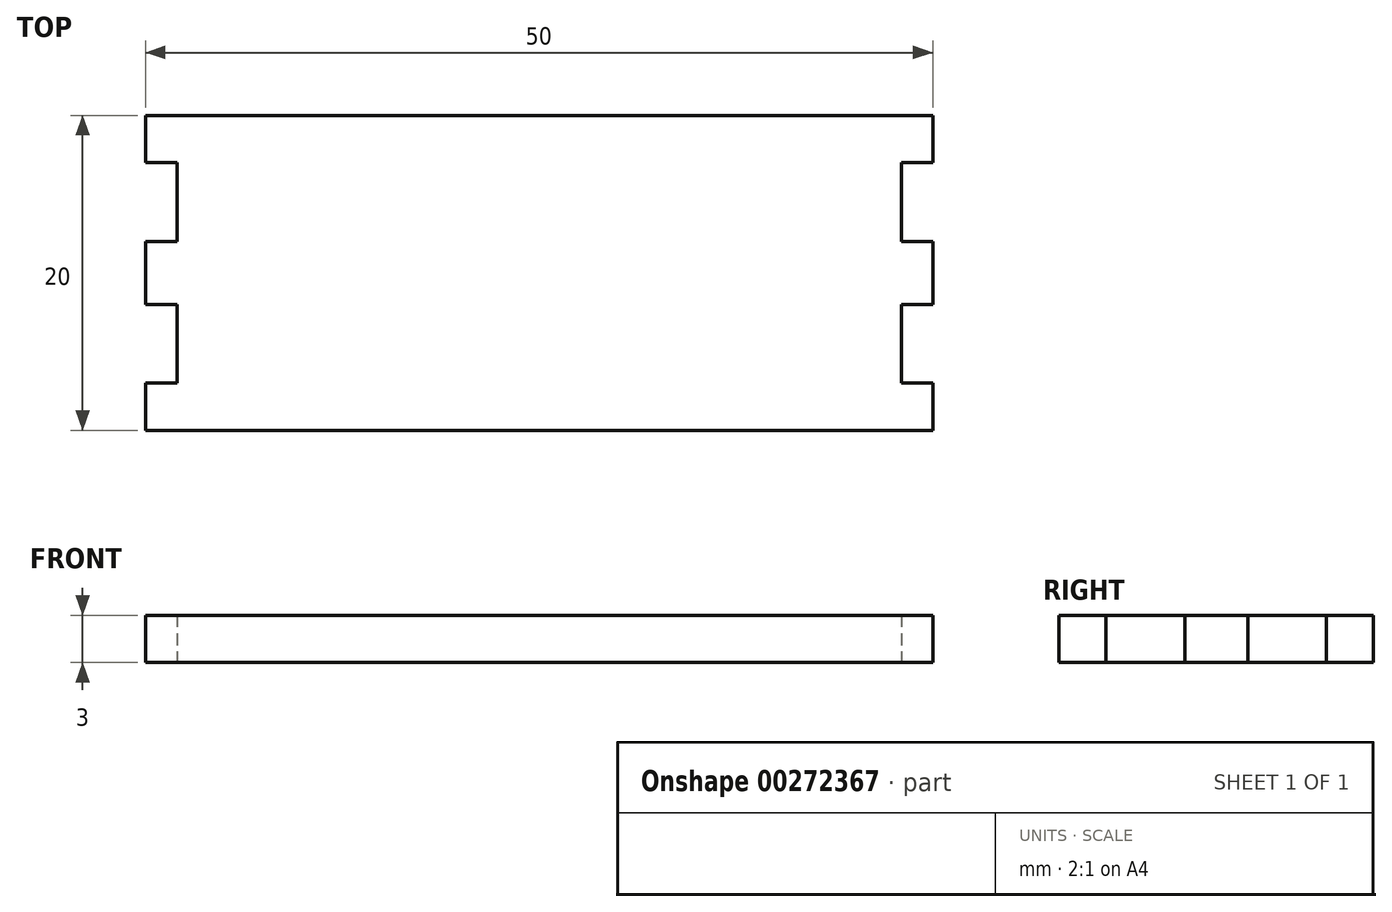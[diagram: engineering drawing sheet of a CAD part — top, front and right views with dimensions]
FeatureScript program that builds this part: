
annotation { "Feature Type Name" : "Feature", "Feature Type Description" : "" }
export const myFeature = defineFeature(function(context is Context, id is Id, definition is map)
    precondition{}
    {
        {
            var Q0;
            Q0=qCreatedBy(makeId("Top.planeOp"),FACE);
            var sketch = newSketch(context, id + "F0", { "sketchPlane" : qUnion([Q0])});
            skLineSegment(sketch, "E0.bottom", {"start": v(-25, 10) * mm, "end": v(25, 10) * mm});
            skLineSegment(sketch, "E0.top", {"start": v(-25, -10) * mm, "end": v(25, -10) * mm});
            skPoint(sketch, "E0.middle", {"position": v(0, 0) * mm});
            skLineSegment(sketch, "E1", {"start": v(0, 10) * mm, "end": v(0, -10) * mm, "construction": true});
            skLineSegment(sketch, "E2", {"start": v(-25, 0) * mm, "end": v(25, 0) * mm, "construction": true});
            skLineSegment(sketch, "E3", {"start": v(-25, 10) * mm, "end": v(-25, 7) * mm});
            skLineSegment(sketch, "E4", {"start": v(-25, 7) * mm, "end": v(-23, 7) * mm});
            skLineSegment(sketch, "E5", {"start": v(-23, 7) * mm, "end": v(-23, 2) * mm});
            skLineSegment(sketch, "E6", {"start": v(-23, 2) * mm, "end": v(-25, 2) * mm});
            skLineSegment(sketch, "E7", {"start": v(-25, 2) * mm, "end": v(-25, 0) * mm});
            skLineSegment(sketch, "E8.MirrorCS", {"start": v(-25, -2) * mm, "end": v(-25, 0) * mm});
            skLineSegment(sketch, "E9.MirrorCS", {"start": v(-23, -2) * mm, "end": v(-25, -2) * mm});
            skLineSegment(sketch, "E10.MirrorCS", {"start": v(-23, -7) * mm, "end": v(-23, -2) * mm});
            skLineSegment(sketch, "E11.MirrorCS", {"start": v(-25, -10) * mm, "end": v(-25, -7) * mm});
            skLineSegment(sketch, "E12.MirrorCS", {"start": v(-25, -7) * mm, "end": v(-23, -7) * mm});
            skLineSegment(sketch, "E13.MirrorCS", {"start": v(25, -10) * mm, "end": v(25, -7) * mm});
            skLineSegment(sketch, "E14.MirrorCS", {"start": v(25, -7) * mm, "end": v(23, -7) * mm});
            skLineSegment(sketch, "E15.MirrorCS", {"start": v(23, -7) * mm, "end": v(23, -2) * mm});
            skLineSegment(sketch, "E16.MirrorCS", {"start": v(23, -2) * mm, "end": v(25, -2) * mm});
            skLineSegment(sketch, "E17.MirrorCS", {"start": v(25, -2) * mm, "end": v(25, 0) * mm});
            skLineSegment(sketch, "E18.MirrorCS", {"start": v(25, 2) * mm, "end": v(25, 0) * mm});
            skLineSegment(sketch, "E19.MirrorCS", {"start": v(23, 2) * mm, "end": v(25, 2) * mm});
            skLineSegment(sketch, "E20.MirrorCS", {"start": v(23, 7) * mm, "end": v(23, 2) * mm});
            skLineSegment(sketch, "E21.MirrorCS", {"start": v(25, 10) * mm, "end": v(25, 7) * mm});
            skLineSegment(sketch, "E22.MirrorCS", {"start": v(25, 7) * mm, "end": v(23, 7) * mm});
            skSolve(sketch);
        }
        {
            var Q0;
            Q0=makeQuery(id+"F0.imprint","IMPRINT",FACE,{"disambiguationData":[TD([[makeQuery(id+"F0.imprint","IMPRINT",EDGE,{"derivedFrom":sQuery(id+"F0.wireOp",EDGE,"E0.bottom")}),-1.0]])]});
            extrude(context, id + "F1", {"entities" : qUnion([Q0]), "depth" : 3 * mm});
        }
    });
